# Revit family: SHR800
name_source: partatom
category: Mechanical Equipment
revit_build: Autodesk Revit 2016 (Build: 20170117_1200(x64)
units: mm (PartAtom-declared; Revit-internal decimal feet)

## family parameters
Always vertical = Yes
Cut with Voids When Loaded = No
OmniClass Number = 23.75.00.00
OmniClass Title = Climate Control (HVAC)
Part Type = Normal
Room Calculation Point = No
Round Connector Dimension = Use Diameter
Shared = No
Work Plane-Based = No

## types (2) — shared parameters
Apparent Load = 636 W
Average Airflow = 794 CFM
Current = 5.3 A
Description = Commercial Heat Recovery Ventilators
Load Classification = HVAC
Manufacturer = Fantech
Model = SHR 800
Number of poles = 1
Power Factor = 1
URL = http://www.fantech.net
Voltage = 120 V
Weight = 158 lbs
Width = 506 mm  [stored 1.6601 ft]

## per-type parameters (varying)
| type | BPM | Not Bpm | Product number | construction |
| SHR 800 BPM | Yes | No | 99270, 99301 | 99 |
| SHR 800 | No | Yes | 99270 | 0 |

note: [stored X ft] marks values corroborated as IEEE doubles in the binary element streams (Revit-internal decimal feet)

## geometry (parser evidence)
native form markers: Blend x2, Sweep x3
no freeform markers — native parametric forms only
